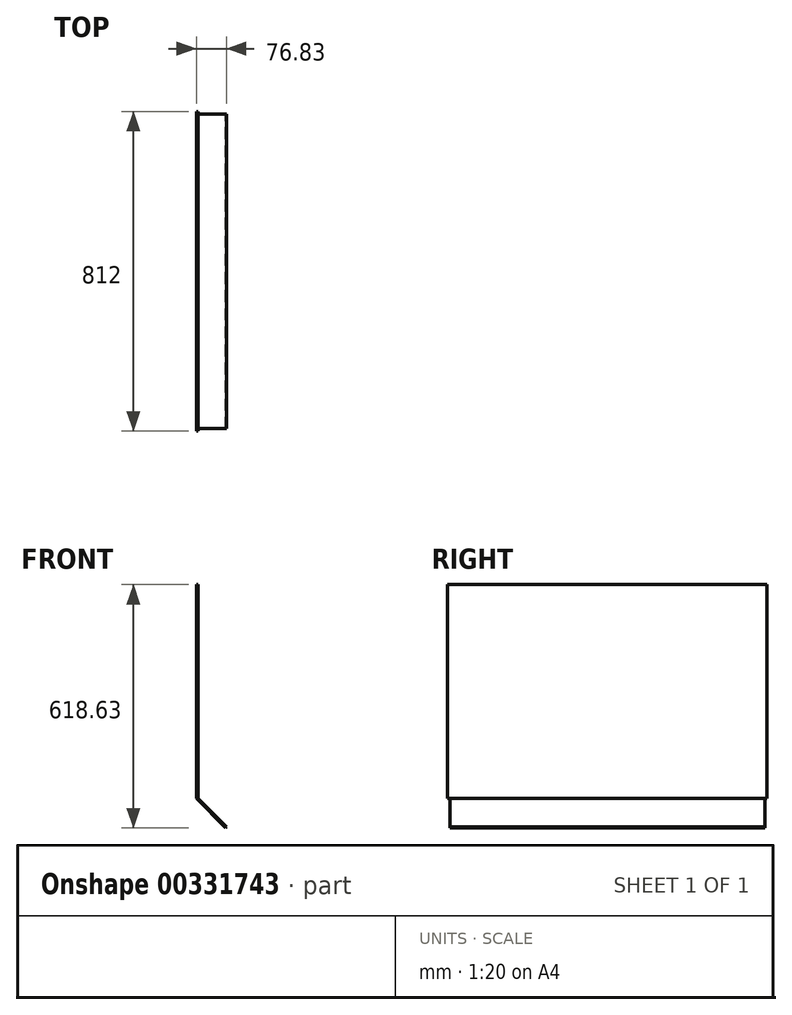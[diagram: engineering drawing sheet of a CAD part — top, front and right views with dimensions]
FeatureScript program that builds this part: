
annotation { "Feature Type Name" : "Feature", "Feature Type Description" : "" }
export const myFeature = defineFeature(function(context is Context, id is Id, definition is map)
    precondition{}
    {
        {
            var Q0;
            Q0=qCreatedBy(makeId("Front.planeOp"),FACE);
            var sketch = newSketch(context, id + "F0", { "sketchPlane" : qUnion([Q0])});
            skLineSegment(sketch, "E0.bottom", {"start": v(0, 543) * mm, "end": v(4, 543) * mm});
            skLineSegment(sketch, "E0.top", {"start": v(0, 0) * mm, "end": v(4, 0) * mm});
            skLineSegment(sketch, "E0.left", {"start": v(0, 543) * mm, "end": v(0, 0) * mm});
            skLineSegment(sketch, "E0.right", {"start": v(4, 543) * mm, "end": v(4, 0) * mm});
            skLineSegment(sketch, "E1", {"start": v(0, 0) * mm, "end": v(73.97, -75.63) * mm});
            skLineSegment(sketch, "E2", {"start": v(73.97, -75.63) * mm, "end": v(76.83, -72.83) * mm});
            skLineSegment(sketch, "E3", {"start": v(76.83, -72.83) * mm, "end": v(4, 0) * mm});
            skSolve(sketch);
        }
        {
            var Q0;
            Q0 = qSketchRegion(id + "F0", true);
            extrude(context, id + "F1", {"entities" : qUnion([Q0]), "depth" : 800 * mm});
        }
        {
            var Q0;
            Q0=makeQuery(id+"F1.opExtrude","SWEPT_FACE",FACE,{"disambiguationData":[OSD([sQuery(id+"F0.wireOp",EDGE,"E0.right")])]});
            var sketch = newSketch(context, id + "F2", { "sketchPlane" : qUnion([Q0])});
            skLineSegment(sketch, "E4.bottom", {"start": v(0, 543) * mm, "end": v(6, 543) * mm});
            skLineSegment(sketch, "E4.top", {"start": v(0, 0) * mm, "end": v(6, 0) * mm});
            skLineSegment(sketch, "E4.left", {"start": v(0, 543) * mm, "end": v(0, 0) * mm});
            skLineSegment(sketch, "E4.right", {"start": v(6, 543) * mm, "end": v(6, 0) * mm});
            skLineSegment(sketch, "E5.bottom", {"start": v(-800, 543) * mm, "end": v(-806, 543) * mm});
            skLineSegment(sketch, "E5.top", {"start": v(-800, 0) * mm, "end": v(-806, 0) * mm});
            skLineSegment(sketch, "E5.left", {"start": v(-800, 543) * mm, "end": v(-800, 0) * mm});
            skLineSegment(sketch, "E5.right", {"start": v(-806, 543) * mm, "end": v(-806, 0) * mm});
            skSolve(sketch);
        }
        {
            var Q0;
            Q0=makeQuery(id+"F2.imprint","IMPRINT",FACE,{"disambiguationData":[TD([[makeQuery(id+"F2.imprint","IMPRINT",EDGE,{"derivedFrom":sQuery(id+"F2.wireOp",EDGE,"E5.bottom")}),1.0]])]});
            var Q1;
            Q1=makeQuery(id+"F2.imprint","IMPRINT",FACE,{"disambiguationData":[TD([[makeQuery(id+"F2.imprint","IMPRINT",EDGE,{"derivedFrom":sQuery(id+"F2.wireOp",EDGE,"E4.bottom")}),-1.0]])]});
            extrude(context, id + "F3", {"entities" : qUnion([Q0, Q1]), "operationType" : NewBodyOperationType.ADD, "oppositeDirection" : true, "depth" : 4 * mm});
        }
    });
